# Revit family: RN 81033 Optipress-Aquaplus-Übergang
name_source: partatom
category: Rohrformteile
units: mm (PartAtom-declared; Revit-internal decimal feet)

## family parameters
Arbeitsebenenbasiert = Nein
Beim Laden mit Abzugskörper schneiden = Nein
Bemaßung runder Anschluss = Durchmesser verwenden
Gemeinsam genutzt = Nein
Immer vertikal = Ja
Teiletyp = Verbindung

## types (21) — shared parameters
1.010.00.2 Blattnummer der Richtlinie = 29
1.010.00.3 Ausgabedatum (Monat) der Richtlinie = 201308
1.010.00.4 Herstellername = R. Nussbaum AG
1.010.00.5 Revisionsdatum der Datei = 20190521
1.010.00.6 Webadresse des Herstellers = http://www.nussbaum.ch
1.100.00.4 Produktbezeichnung = Versorgung
1.110.00.2 Index = 4
1.110.00.4 Produktbezeichnung = Optipress
1.960/3L.00.8 Link (URL) = https://www.nussbaum.ch
29.700.00.4 Produktname = Optipress-Aquaplus-Übergang, mit Innengewinde
29.700.00.5 Produktkennung = 2
29.700.00.6 Querschnittsform = 1
29.700.00.7 Nennweitensystem = DN
29.700.00.8 Nenndrucksystem = PN
29.710.02.4 Nenndruck = 16
29.710.02.5 max. zul. Überdruck [hPa] = 1600
29.710.02.7 max. zul. Dauer-Betriebsdruck [hPa] = 1600
29.710.02.9 max. zul. Dauer-Betriebstemperatur [°C] = 95
Connector Visibility = Nein
EnclosingSpace Visibility = Nein

## per-type parameters (varying)
- 81033.19, Optipress-Aquaplus-Übergang, mit Innengewinde, DN=10, L=32, Rp=3/8: 1.800.00.3 TGA-Nummer=01900400000000000000000000000000000000000000000022000000000000000019; 1.810.00.3 Hersteller-Bestellnummer=81033.19; 1.810.00.4 DATANORM-Nummer=81033.19; 1.810.00.6 GTIN-Nummer=7612945021304; 29.710.02.10 Formstück-Gewicht [kg]=0.031; 29.710.02.3 Benennung=Optipress-Aquaplus-Übergang, mit Innengewinde, DN=10, L=32, Rp=3/8; CONNECTOR0_DIAMETER_dX_0r=10 mm  [stored 0.0328084 ft]; CONNECTOR0_dX_01=18 mm; CONNECTOR0_ref_dX=18 mm; CONNECTOR1_DIAMETER_dX_0r=10 mm  [stored 0.0328084 ft]; CONNECTOR1_dX_00=20 mm; CONNECTOR1_dX_01=32 mm; CONNECTOR1_ref_dX=20 mm; R. Nussbaum AG 81033.19 de Visibility=Ja; R. Nussbaum AG 81033.20 de Visibility=Nein; R. Nussbaum AG 81033.21 de Visibility=Nein; R. Nussbaum AG 81033.22 de Visibility=Nein; R. Nussbaum AG 81033.23 de Visibility=Nein; R. Nussbaum AG 81033.24 de Visibility=Nein; R. Nussbaum AG 81033.25 de Visibility=Nein; R. Nussbaum AG 81033.26 de Visibility=Nein; R. Nussbaum AG 81033.27 de Visibility=Nein; R. Nussbaum AG 81033.28 de Visibility=Nein; R. Nussbaum AG 81033.29 de Visibility=Nein; R. Nussbaum AG 81033.30 de Visibility=Nein; R. Nussbaum AG 81033.31 de Visibility=Nein; R. Nussbaum AG 81033.32 de Visibility=Nein; R. Nussbaum AG 81033.33 de Visibility=Nein; R. Nussbaum AG 81033.34 de Visibility=Nein; R. Nussbaum AG 81033.35 de Visibility=Nein; R. Nussbaum AG 81033.36 de Visibility=Nein; R. Nussbaum AG 81033.37 de Visibility=Nein; R. Nussbaum AG 81033.38 de Visibility=Nein; R. Nussbaum AG 81033.39 de Visibility=Nein
- 81033.21, Optipress-Aquaplus-Übergang, mit Innengewinde, DN=15x10, L=37, Rp=3/8: 1.800.00.3 TGA-Nummer=01900400000000000000000000000000000000000000000022000000000000000020; 1.810.00.3 Hersteller-Bestellnummer=81033.21; 1.810.00.4 DATANORM-Nummer=81033.21; 1.810.00.6 GTIN-Nummer=7612945021328; 29.710.02.10 Formstück-Gewicht [kg]=0.037; 29.710.02.3 Benennung=Optipress-Aquaplus-Übergang, mit Innengewinde, DN=15x10, L=37, Rp=3/8; CONNECTOR0_DIAMETER_dX_0r=12 mm  [stored 0.0393701 ft]; CONNECTOR0_dX_01=22 mm; CONNECTOR0_ref_dX=22 mm; CONNECTOR1_DIAMETER_dX_0r=12 mm  [stored 0.0393701 ft]; CONNECTOR1_dX_00=27 mm; CONNECTOR1_dX_01=37 mm; CONNECTOR1_ref_dX=27 mm; R. Nussbaum AG 81033.19 de Visibility=Nein; R. Nussbaum AG 81033.20 de Visibility=Nein; R. Nussbaum AG 81033.21 de Visibility=Ja; R. Nussbaum AG 81033.22 de Visibility=Nein; R. Nussbaum AG 81033.23 de Visibility=Nein; R. Nussbaum AG 81033.24 de Visibility=Nein; R. Nussbaum AG 81033.25 de Visibility=Nein; R. Nussbaum AG 81033.26 de Visibility=Nein; R. Nussbaum AG 81033.27 de Visibility=Nein; R. Nussbaum AG 81033.28 de Visibility=Nein; R. Nussbaum AG 81033.29 de Visibility=Nein; R. Nussbaum AG 81033.30 de Visibility=Nein; R. Nussbaum AG 81033.31 de Visibility=Nein; R. Nussbaum AG 81033.32 de Visibility=Nein; R. Nussbaum AG 81033.33 de Visibility=Nein; R. Nussbaum AG 81033.34 de Visibility=Nein; R. Nussbaum AG 81033.35 de Visibility=Nein; R. Nussbaum AG 81033.36 de Visibility=Nein; R. Nussbaum AG 81033.37 de Visibility=Nein; R. Nussbaum AG 81033.38 de Visibility=Nein; R. Nussbaum AG 81033.39 de Visibility=Nein
- 81033.22, Optipress-Aquaplus-Übergang, mit Innengewinde, DN=12x15, L=44, Rp=½: 1.800.00.3 TGA-Nummer=01900400000000000000000000000000000000000000000022000000000000000021; 1.810.00.3 Hersteller-Bestellnummer=81033.22; 1.810.00.4 DATANORM-Nummer=81033.22; 1.810.00.5 StLB-Nummer=267.132; 1.810.00.6 GTIN-Nummer=7612945021335; 29.710.02.10 Formstück-Gewicht [kg]=0.062; 29.710.02.3 Benennung=Optipress-Aquaplus-Übergang, mit Innengewinde, DN=12x15, L=44, Rp=½; CONNECTOR0_DIAMETER_dX_0r=12 mm  [stored 0.0393701 ft]; CONNECTOR0_dX_01=22 mm; CONNECTOR0_ref_dX=22 mm; CONNECTOR1_DIAMETER_dX_0r=15 mm; CONNECTOR1_dX_00=31 mm  [stored 0.101706 ft]; CONNECTOR1_dX_01=44 mm; CONNECTOR1_ref_dX=31 mm  [stored 0.101706 ft]; R. Nussbaum AG 81033.19 de Visibility=Nein; R. Nussbaum AG 81033.20 de Visibility=Nein; R. Nussbaum AG 81033.21 de Visibility=Nein; R. Nussbaum AG 81033.22 de Visibility=Ja; R. Nussbaum AG 81033.23 de Visibility=Nein; R. Nussbaum AG 81033.24 de Visibility=Nein; R. Nussbaum AG 81033.25 de Visibility=Nein; R. Nussbaum AG 81033.26 de Visibility=Nein; R. Nussbaum AG 81033.27 de Visibility=Nein; R. Nussbaum AG 81033.28 de Visibility=Nein; R. Nussbaum AG 81033.29 de Visibility=Nein; R. Nussbaum AG 81033.30 de Visibility=Nein; R. Nussbaum AG 81033.31 de Visibility=Nein; R. Nussbaum AG 81033.32 de Visibility=Nein; R. Nussbaum AG 81033.33 de Visibility=Nein; R. Nussbaum AG 81033.34 de Visibility=Nein; R. Nussbaum AG 81033.35 de Visibility=Nein; R. Nussbaum AG 81033.36 de Visibility=Nein; R. Nussbaum AG 81033.37 de Visibility=Nein; R. Nussbaum AG 81033.38 de Visibility=Nein; R. Nussbaum AG 81033.39 de Visibility=Nein
- 81033.23, Optipress-Aquaplus-Übergang, mit Innengewinde, DN=15, L=43, Rp=½: 1.800.00.3 TGA-Nummer=01900400000000000000000000000000000000000000000022000000000000000022; 1.810.00.3 Hersteller-Bestellnummer=81033.23; 1.810.00.4 DATANORM-Nummer=81033.23; 1.810.00.5 StLB-Nummer=267.133; 1.810.00.6 GTIN-Nummer=7612945021342; 29.710.02.10 Formstück-Gewicht [kg]=0.063; 29.710.02.3 Benennung=Optipress-Aquaplus-Übergang, mit Innengewinde, DN=15, L=43, Rp=½; CONNECTOR0_DIAMETER_dX_0r=15 mm; CONNECTOR0_dX_01=22 mm; CONNECTOR0_ref_dX=22 mm; CONNECTOR1_DIAMETER_dX_0r=15 mm; CONNECTOR1_dX_00=30 mm  [stored 0.0984252 ft]; CONNECTOR1_dX_01=43 mm  [stored 0.141076 ft]; CONNECTOR1_ref_dX=30 mm  [stored 0.0984252 ft]; R. Nussbaum AG 81033.19 de Visibility=Nein; R. Nussbaum AG 81033.20 de Visibility=Nein; R. Nussbaum AG 81033.21 de Visibility=Nein; R. Nussbaum AG 81033.22 de Visibility=Nein; R. Nussbaum AG 81033.23 de Visibility=Ja; R. Nussbaum AG 81033.24 de Visibility=Nein; R. Nussbaum AG 81033.25 de Visibility=Nein; R. Nussbaum AG 81033.26 de Visibility=Nein; R. Nussbaum AG 81033.27 de Visibility=Nein; R. Nussbaum AG 81033.28 de Visibility=Nein; R. Nussbaum AG 81033.29 de Visibility=Nein; R. Nussbaum AG 81033.30 de Visibility=Nein; R. Nussbaum AG 81033.31 de Visibility=Nein; R. Nussbaum AG 81033.32 de Visibility=Nein; R. Nussbaum AG 81033.33 de Visibility=Nein; R. Nussbaum AG 81033.34 de Visibility=Nein; R. Nussbaum AG 81033.35 de Visibility=Nein; R. Nussbaum AG 81033.36 de Visibility=Nein; R. Nussbaum AG 81033.37 de Visibility=Nein; R. Nussbaum AG 81033.38 de Visibility=Nein; R. Nussbaum AG 81033.39 de Visibility=Nein
- 81033.24, Optipress-Aquaplus-Übergang, mit Innengewinde, DN=15x20, L=45, Rp=¾: 1.800.00.3 TGA-Nummer=01900400000000000000000000000000000000000000000022000000000000000023; 1.810.00.3 Hersteller-Bestellnummer=81033.24; 1.810.00.4 DATANORM-Nummer=81033.24; 1.810.00.6 GTIN-Nummer=7612945021359; 29.710.02.10 Formstück-Gewicht [kg]=0.076; 29.710.02.3 Benennung=Optipress-Aquaplus-Übergang, mit Innengewinde, DN=15x20, L=45, Rp=¾; CONNECTOR0_DIAMETER_dX_0r=15 mm; CONNECTOR0_dX_01=22 mm; CONNECTOR0_ref_dX=22 mm; CONNECTOR1_DIAMETER_dX_0r=20 mm; CONNECTOR1_dX_00=30 mm  [stored 0.0984252 ft]; CONNECTOR1_dX_01=45 mm; CONNECTOR1_ref_dX=30 mm  [stored 0.0984252 ft]; R. Nussbaum AG 81033.19 de Visibility=Nein; R. Nussbaum AG 81033.20 de Visibility=Nein; R. Nussbaum AG 81033.21 de Visibility=Nein; R. Nussbaum AG 81033.22 de Visibility=Nein; R. Nussbaum AG 81033.23 de Visibility=Nein; R. Nussbaum AG 81033.24 de Visibility=Ja; R. Nussbaum AG 81033.25 de Visibility=Nein; R. Nussbaum AG 81033.26 de Visibility=Nein; R. Nussbaum AG 81033.27 de Visibility=Nein; R. Nussbaum AG 81033.28 de Visibility=Nein; R. Nussbaum AG 81033.29 de Visibility=Nein; R. Nussbaum AG 81033.30 de Visibility=Nein; R. Nussbaum AG 81033.31 de Visibility=Nein; R. Nussbaum AG 81033.32 de Visibility=Nein; R. Nussbaum AG 81033.33 de Visibility=Nein; R. Nussbaum AG 81033.34 de Visibility=Nein; R. Nussbaum AG 81033.35 de Visibility=Nein; R. Nussbaum AG 81033.36 de Visibility=Nein; R. Nussbaum AG 81033.37 de Visibility=Nein; R. Nussbaum AG 81033.38 de Visibility=Nein; R. Nussbaum AG 81033.39 de Visibility=Nein
- 81033.25, Optipress-Aquaplus-Übergang, mit Innengewinde, DN=20, L=47, Rp=¾: 1.800.00.3 TGA-Nummer=01900400000000000000000000000000000000000000000022000000000000000024; 1.810.00.3 Hersteller-Bestellnummer=81033.25; 1.810.00.4 DATANORM-Nummer=81033.25; 1.810.00.5 StLB-Nummer=267.134; 1.810.00.6 GTIN-Nummer=7612945021366; 29.710.02.10 Formstück-Gewicht [kg]=0.082; 29.710.02.3 Benennung=Optipress-Aquaplus-Übergang, mit Innengewinde, DN=20, L=47, Rp=¾; CONNECTOR0_DIAMETER_dX_0r=20 mm; CONNECTOR0_dX_01=24 mm; CONNECTOR0_ref_dX=24 mm; CONNECTOR1_DIAMETER_dX_0r=20 mm; CONNECTOR1_dX_00=32 mm; CONNECTOR1_dX_01=47 mm; CONNECTOR1_ref_dX=32 mm; R. Nussbaum AG 81033.19 de Visibility=Nein; R. Nussbaum AG 81033.20 de Visibility=Nein; R. Nussbaum AG 81033.21 de Visibility=Nein; R. Nussbaum AG 81033.22 de Visibility=Nein; R. Nussbaum AG 81033.23 de Visibility=Nein; R. Nussbaum AG 81033.24 de Visibility=Nein; R. Nussbaum AG 81033.25 de Visibility=Ja; R. Nussbaum AG 81033.26 de Visibility=Nein; R. Nussbaum AG 81033.27 de Visibility=Nein; R. Nussbaum AG 81033.28 de Visibility=Nein; R. Nussbaum AG 81033.29 de Visibility=Nein; R. Nussbaum AG 81033.30 de Visibility=Nein; R. Nussbaum AG 81033.31 de Visibility=Nein; R. Nussbaum AG 81033.32 de Visibility=Nein; R. Nussbaum AG 81033.33 de Visibility=Nein; R. Nussbaum AG 81033.34 de Visibility=Nein; R. Nussbaum AG 81033.35 de Visibility=Nein; R. Nussbaum AG 81033.36 de Visibility=Nein; R. Nussbaum AG 81033.37 de Visibility=Nein; R. Nussbaum AG 81033.38 de Visibility=Nein; R. Nussbaum AG 81033.39 de Visibility=Nein
- 81033.26, Optipress-Aquaplus-Übergang, mit Innengewinde, DN=20x25, L=52, Rp=1: 1.800.00.3 TGA-Nummer=01900400000000000000000000000000000000000000000022000000000000000025; 1.810.00.3 Hersteller-Bestellnummer=81033.26; 1.810.00.4 DATANORM-Nummer=81033.26; 1.810.00.6 GTIN-Nummer=7612945021373; 29.710.02.10 Formstück-Gewicht [kg]=0.131; 29.710.02.3 Benennung=Optipress-Aquaplus-Übergang, mit Innengewinde, DN=20x25, L=52, Rp=1; CONNECTOR0_DIAMETER_dX_0r=20 mm; CONNECTOR0_dX_01=24 mm; CONNECTOR0_ref_dX=24 mm; CONNECTOR1_DIAMETER_dX_0r=25 mm  [stored 0.082021 ft]; CONNECTOR1_dX_00=35 mm; CONNECTOR1_dX_01=52 mm; CONNECTOR1_ref_dX=35 mm; R. Nussbaum AG 81033.19 de Visibility=Nein; R. Nussbaum AG 81033.20 de Visibility=Nein; R. Nussbaum AG 81033.21 de Visibility=Nein; R. Nussbaum AG 81033.22 de Visibility=Nein; R. Nussbaum AG 81033.23 de Visibility=Nein; R. Nussbaum AG 81033.24 de Visibility=Nein; R. Nussbaum AG 81033.25 de Visibility=Nein; R. Nussbaum AG 81033.26 de Visibility=Ja; R. Nussbaum AG 81033.27 de Visibility=Nein; R. Nussbaum AG 81033.28 de Visibility=Nein; R. Nussbaum AG 81033.29 de Visibility=Nein; R. Nussbaum AG 81033.30 de Visibility=Nein; R. Nussbaum AG 81033.31 de Visibility=Nein; R. Nussbaum AG 81033.32 de Visibility=Nein; R. Nussbaum AG 81033.33 de Visibility=Nein; R. Nussbaum AG 81033.34 de Visibility=Nein; R. Nussbaum AG 81033.35 de Visibility=Nein; R. Nussbaum AG 81033.36 de Visibility=Nein; R. Nussbaum AG 81033.37 de Visibility=Nein; R. Nussbaum AG 81033.38 de Visibility=Nein; R. Nussbaum AG 81033.39 de Visibility=Nein
- 81033.27, Optipress-Aquaplus-Übergang, mit Innengewinde, DN=25x20, L=47, Rp=¾: 1.800.00.3 TGA-Nummer=01900400000000000000000000000000000000000000000022000000000000000026; 1.810.00.3 Hersteller-Bestellnummer=81033.27; 1.810.00.4 DATANORM-Nummer=81033.27; 1.810.00.6 GTIN-Nummer=7612945021380; 29.710.02.10 Formstück-Gewicht [kg]=0.095; 29.710.02.3 Benennung=Optipress-Aquaplus-Übergang, mit Innengewinde, DN=25x20, L=47, Rp=¾; CONNECTOR0_DIAMETER_dX_0r=25 mm  [stored 0.082021 ft]; CONNECTOR0_dX_01=24 mm; CONNECTOR0_ref_dX=24 mm; CONNECTOR1_DIAMETER_dX_0r=20 mm; CONNECTOR1_dX_00=32 mm; CONNECTOR1_dX_01=47 mm; CONNECTOR1_ref_dX=32 mm; R. Nussbaum AG 81033.19 de Visibility=Nein; R. Nussbaum AG 81033.20 de Visibility=Nein; R. Nussbaum AG 81033.21 de Visibility=Nein; R. Nussbaum AG 81033.22 de Visibility=Nein; R. Nussbaum AG 81033.23 de Visibility=Nein; R. Nussbaum AG 81033.24 de Visibility=Nein; R. Nussbaum AG 81033.25 de Visibility=Nein; R. Nussbaum AG 81033.26 de Visibility=Nein; R. Nussbaum AG 81033.27 de Visibility=Ja; R. Nussbaum AG 81033.28 de Visibility=Nein; R. Nussbaum AG 81033.29 de Visibility=Nein; R. Nussbaum AG 81033.30 de Visibility=Nein; R. Nussbaum AG 81033.31 de Visibility=Nein; R. Nussbaum AG 81033.32 de Visibility=Nein; R. Nussbaum AG 81033.33 de Visibility=Nein; R. Nussbaum AG 81033.34 de Visibility=Nein; R. Nussbaum AG 81033.35 de Visibility=Nein; R. Nussbaum AG 81033.36 de Visibility=Nein; R. Nussbaum AG 81033.37 de Visibility=Nein; R. Nussbaum AG 81033.38 de Visibility=Nein; R. Nussbaum AG 81033.39 de Visibility=Nein
- 81033.28, Optipress-Aquaplus-Übergang, mit Innengewinde, DN=25x15, L=44, Rp=½: 1.800.00.3 TGA-Nummer=01900400000000000000000000000000000000000000000022000000000000000027; 1.810.00.3 Hersteller-Bestellnummer=81033.28; 1.810.00.4 DATANORM-Nummer=81033.28; 1.810.00.6 GTIN-Nummer=7612945682727; 29.710.02.10 Formstück-Gewicht [kg]=0.089; 29.710.02.3 Benennung=Optipress-Aquaplus-Übergang, mit Innengewinde, DN=25x15, L=44, Rp=½; CONNECTOR0_DIAMETER_dX_0r=25 mm  [stored 0.082021 ft]; CONNECTOR0_dX_01=24 mm; CONNECTOR0_ref_dX=24 mm; CONNECTOR1_DIAMETER_dX_0r=15 mm; CONNECTOR1_dX_00=31 mm  [stored 0.101706 ft]; CONNECTOR1_dX_01=44 mm; CONNECTOR1_ref_dX=31 mm  [stored 0.101706 ft]; R. Nussbaum AG 81033.19 de Visibility=Nein; R. Nussbaum AG 81033.20 de Visibility=Nein; R. Nussbaum AG 81033.21 de Visibility=Nein; R. Nussbaum AG 81033.22 de Visibility=Nein; R. Nussbaum AG 81033.23 de Visibility=Nein; R. Nussbaum AG 81033.24 de Visibility=Nein; R. Nussbaum AG 81033.25 de Visibility=Nein; R. Nussbaum AG 81033.26 de Visibility=Nein; R. Nussbaum AG 81033.27 de Visibility=Nein; R. Nussbaum AG 81033.28 de Visibility=Ja; R. Nussbaum AG 81033.29 de Visibility=Nein; R. Nussbaum AG 81033.30 de Visibility=Nein; R. Nussbaum AG 81033.31 de Visibility=Nein; R. Nussbaum AG 81033.32 de Visibility=Nein; R. Nussbaum AG 81033.33 de Visibility=Nein; R. Nussbaum AG 81033.34 de Visibility=Nein; R. Nussbaum AG 81033.35 de Visibility=Nein; R. Nussbaum AG 81033.36 de Visibility=Nein; R. Nussbaum AG 81033.37 de Visibility=Nein; R. Nussbaum AG 81033.38 de Visibility=Nein; R. Nussbaum AG 81033.39 de Visibility=Nein
- 81033.29, Optipress-Aquaplus-Übergang, mit Innengewinde, DN=20, L=52, Rp=1: 1.800.00.3 TGA-Nummer=01900400000000000000000000000000000000000000000022000000000000000028; 1.810.00.3 Hersteller-Bestellnummer=81033.29; 1.810.00.4 DATANORM-Nummer=81033.29; 1.810.00.5 StLB-Nummer=267.135; 1.810.00.6 GTIN-Nummer=7612945021397; 29.710.02.10 Formstück-Gewicht [kg]=0.124; 29.710.02.3 Benennung=Optipress-Aquaplus-Übergang, mit Innengewinde, DN=20, L=52, Rp=1; CONNECTOR0_DIAMETER_dX_0r=25 mm  [stored 0.082021 ft]; CONNECTOR0_dX_01=24 mm; CONNECTOR0_ref_dX=24 mm; CONNECTOR1_DIAMETER_dX_0r=25 mm  [stored 0.082021 ft]; CONNECTOR1_dX_00=35 mm; CONNECTOR1_dX_01=52 mm; CONNECTOR1_ref_dX=35 mm; R. Nussbaum AG 81033.19 de Visibility=Nein; R. Nussbaum AG 81033.20 de Visibility=Nein; R. Nussbaum AG 81033.21 de Visibility=Nein; R. Nussbaum AG 81033.22 de Visibility=Nein; R. Nussbaum AG 81033.23 de Visibility=Nein; R. Nussbaum AG 81033.24 de Visibility=Nein; R. Nussbaum AG 81033.25 de Visibility=Nein; R. Nussbaum AG 81033.26 de Visibility=Nein; R. Nussbaum AG 81033.27 de Visibility=Nein; R. Nussbaum AG 81033.28 de Visibility=Nein; R. Nussbaum AG 81033.29 de Visibility=Ja; R. Nussbaum AG 81033.30 de Visibility=Nein; R. Nussbaum AG 81033.31 de Visibility=Nein; R. Nussbaum AG 81033.32 de Visibility=Nein; R. Nussbaum AG 81033.33 de Visibility=Nein; R. Nussbaum AG 81033.34 de Visibility=Nein; R. Nussbaum AG 81033.35 de Visibility=Nein; R. Nussbaum AG 81033.36 de Visibility=Nein; R. Nussbaum AG 81033.37 de Visibility=Nein; R. Nussbaum AG 81033.38 de Visibility=Nein; R. Nussbaum AG 81033.39 de Visibility=Nein
- 81033.31, Optipress-Aquaplus-Übergang, mit Innengewinde, DN=32, L=54, Rp=1¼: 1.800.00.3 TGA-Nummer=01900400000000000000000000000000000000000000000022000000000000000029; 1.810.00.3 Hersteller-Bestellnummer=81033.31; 1.810.00.4 DATANORM-Nummer=81033.31; 1.810.00.5 StLB-Nummer=267.136; 1.810.00.6 GTIN-Nummer=7612945021410; 29.710.02.10 Formstück-Gewicht [kg]=0.17; 29.710.02.3 Benennung=Optipress-Aquaplus-Übergang, mit Innengewinde, DN=32, L=54, Rp=1¼; CONNECTOR0_DIAMETER_dX_0r=32 mm; CONNECTOR0_dX_01=26 mm; CONNECTOR0_ref_dX=26 mm; CONNECTOR1_DIAMETER_dX_0r=32 mm; CONNECTOR1_dX_00=35 mm; CONNECTOR1_dX_01=54 mm; CONNECTOR1_ref_dX=35 mm; R. Nussbaum AG 81033.19 de Visibility=Nein; R. Nussbaum AG 81033.20 de Visibility=Nein; R. Nussbaum AG 81033.21 de Visibility=Nein; R. Nussbaum AG 81033.22 de Visibility=Nein; R. Nussbaum AG 81033.23 de Visibility=Nein; R. Nussbaum AG 81033.24 de Visibility=Nein; R. Nussbaum AG 81033.25 de Visibility=Nein; R. Nussbaum AG 81033.26 de Visibility=Nein; R. Nussbaum AG 81033.27 de Visibility=Nein; R. Nussbaum AG 81033.28 de Visibility=Nein; R. Nussbaum AG 81033.29 de Visibility=Nein; R. Nussbaum AG 81033.30 de Visibility=Nein; R. Nussbaum AG 81033.31 de Visibility=Ja; R. Nussbaum AG 81033.32 de Visibility=Nein; R. Nussbaum AG 81033.33 de Visibility=Nein; R. Nussbaum AG 81033.34 de Visibility=Nein; R. Nussbaum AG 81033.35 de Visibility=Nein; R. Nussbaum AG 81033.36 de Visibility=Nein; R. Nussbaum AG 81033.37 de Visibility=Nein; R. Nussbaum AG 81033.38 de Visibility=Nein; R. Nussbaum AG 81033.39 de Visibility=Nein
- 81033.32, Optipress-Aquaplus-Übergang, mit Innengewinde, DN=40x32, L=61, Rp=1¼: 1.800.00.3 TGA-Nummer=01900400000000000000000000000000000000000000000022000000000000000030; 1.810.00.3 Hersteller-Bestellnummer=81033.32; 1.810.00.4 DATANORM-Nummer=81033.32; 1.810.00.6 GTIN-Nummer=7612945021427; 29.710.02.10 Formstück-Gewicht [kg]=0.22; 29.710.02.3 Benennung=Optipress-Aquaplus-Übergang, mit Innengewinde, DN=40x32, L=61, Rp=1¼; CONNECTOR0_DIAMETER_dX_0r=40 mm; CONNECTOR0_dX_01=36 mm; CONNECTOR0_ref_dX=36 mm; CONNECTOR1_DIAMETER_dX_0r=32 mm; CONNECTOR1_dX_00=42 mm; CONNECTOR1_dX_01=61 mm; CONNECTOR1_ref_dX=42 mm; R. Nussbaum AG 81033.19 de Visibility=Nein; R. Nussbaum AG 81033.20 de Visibility=Nein; R. Nussbaum AG 81033.21 de Visibility=Nein; R. Nussbaum AG 81033.22 de Visibility=Nein; R. Nussbaum AG 81033.23 de Visibility=Nein; R. Nussbaum AG 81033.24 de Visibility=Nein; R. Nussbaum AG 81033.25 de Visibility=Nein; R. Nussbaum AG 81033.26 de Visibility=Nein; R. Nussbaum AG 81033.27 de Visibility=Nein; R. Nussbaum AG 81033.28 de Visibility=Nein; R. Nussbaum AG 81033.29 de Visibility=Nein; R. Nussbaum AG 81033.30 de Visibility=Nein; R. Nussbaum AG 81033.31 de Visibility=Nein; R. Nussbaum AG 81033.32 de Visibility=Ja; R. Nussbaum AG 81033.33 de Visibility=Nein; R. Nussbaum AG 81033.34 de Visibility=Nein; R. Nussbaum AG 81033.35 de Visibility=Nein; R. Nussbaum AG 81033.36 de Visibility=Nein; R. Nussbaum AG 81033.37 de Visibility=Nein; R. Nussbaum AG 81033.38 de Visibility=Nein; R. Nussbaum AG 81033.39 de Visibility=Nein
- 81033.33, Optipress-Aquaplus-Übergang, mit Innengewinde, DN=40, L=69, Rp=1½: 1.800.00.3 TGA-Nummer=01900400000000000000000000000000000000000000000022000000000000000031; 1.810.00.3 Hersteller-Bestellnummer=81033.33; 1.810.00.4 DATANORM-Nummer=81033.33; 1.810.00.5 StLB-Nummer=267.137; 1.810.00.6 GTIN-Nummer=7612945021434; 29.710.02.10 Formstück-Gewicht [kg]=0.267; 29.710.02.3 Benennung=Optipress-Aquaplus-Übergang, mit Innengewinde, DN=40, L=69, Rp=1½; CONNECTOR0_DIAMETER_dX_0r=40 mm; CONNECTOR0_dX_01=36 mm; CONNECTOR0_ref_dX=36 mm; CONNECTOR1_DIAMETER_dX_0r=32 mm; CONNECTOR1_dX_00=50 mm; CONNECTOR1_dX_01=69 mm; CONNECTOR1_ref_dX=50 mm; R. Nussbaum AG 81033.19 de Visibility=Nein; R. Nussbaum AG 81033.20 de Visibility=Nein; R. Nussbaum AG 81033.21 de Visibility=Nein; R. Nussbaum AG 81033.22 de Visibility=Nein; R. Nussbaum AG 81033.23 de Visibility=Nein; R. Nussbaum AG 81033.24 de Visibility=Nein; R. Nussbaum AG 81033.25 de Visibility=Nein; R. Nussbaum AG 81033.26 de Visibility=Nein; R. Nussbaum AG 81033.27 de Visibility=Nein; R. Nussbaum AG 81033.28 de Visibility=Nein; R. Nussbaum AG 81033.29 de Visibility=Nein; R. Nussbaum AG 81033.30 de Visibility=Nein; R. Nussbaum AG 81033.31 de Visibility=Nein; R. Nussbaum AG 81033.32 de Visibility=Nein; R. Nussbaum AG 81033.33 de Visibility=Ja; R. Nussbaum AG 81033.34 de Visibility=Nein; R. Nussbaum AG 81033.35 de Visibility=Nein; R. Nussbaum AG 81033.36 de Visibility=Nein; R. Nussbaum AG 81033.37 de Visibility=Nein; R. Nussbaum AG 81033.38 de Visibility=Nein; R. Nussbaum AG 81033.39 de Visibility=Nein
- 81033.34, Optipress-Aquaplus-Übergang, mit Innengewinde, DN=50x40, L=71, Rp=1½: 1.800.00.3 TGA-Nummer=01900400000000000000000000000000000000000000000022000000000000000032; 1.810.00.3 Hersteller-Bestellnummer=81033.34; 1.810.00.4 DATANORM-Nummer=81033.34; 1.810.00.6 GTIN-Nummer=7612945682734; 29.710.02.10 Formstück-Gewicht [kg]=0.442; 29.710.02.3 Benennung=Optipress-Aquaplus-Übergang, mit Innengewinde, DN=50x40, L=71, Rp=1½; CONNECTOR0_DIAMETER_dX_0r=50 mm; CONNECTOR0_dX_01=40 mm; CONNECTOR0_ref_dX=40 mm; CONNECTOR1_DIAMETER_dX_0r=40 mm; CONNECTOR1_dX_00=53 mm; CONNECTOR1_dX_01=72 mm; CONNECTOR1_ref_dX=53 mm; R. Nussbaum AG 81033.19 de Visibility=Nein; R. Nussbaum AG 81033.20 de Visibility=Nein; R. Nussbaum AG 81033.21 de Visibility=Nein; R. Nussbaum AG 81033.22 de Visibility=Nein; R. Nussbaum AG 81033.23 de Visibility=Nein; R. Nussbaum AG 81033.24 de Visibility=Nein; R. Nussbaum AG 81033.25 de Visibility=Nein; R. Nussbaum AG 81033.26 de Visibility=Nein; R. Nussbaum AG 81033.27 de Visibility=Nein; R. Nussbaum AG 81033.28 de Visibility=Nein; R. Nussbaum AG 81033.29 de Visibility=Nein; R. Nussbaum AG 81033.30 de Visibility=Nein; R. Nussbaum AG 81033.31 de Visibility=Nein; R. Nussbaum AG 81033.32 de Visibility=Nein; R. Nussbaum AG 81033.33 de Visibility=Nein; R. Nussbaum AG 81033.34 de Visibility=Ja; R. Nussbaum AG 81033.35 de Visibility=Nein; R. Nussbaum AG 81033.36 de Visibility=Nein; R. Nussbaum AG 81033.37 de Visibility=Nein; R. Nussbaum AG 81033.38 de Visibility=Nein; R. Nussbaum AG 81033.39 de Visibility=Nein
- 81033.35, Optipress-Aquaplus-Übergang, mit Innengewinde, DN=50, L=75, Rp=2: 1.800.00.3 TGA-Nummer=01900400000000000000000000000000000000000000000022000000000000000033; 1.810.00.3 Hersteller-Bestellnummer=81033.35; 1.810.00.4 DATANORM-Nummer=81033.35; 1.810.00.5 StLB-Nummer=267.138; 1.810.00.6 GTIN-Nummer=7612945021441; 29.710.02.10 Formstück-Gewicht [kg]=0.461; 29.710.02.3 Benennung=Optipress-Aquaplus-Übergang, mit Innengewinde, DN=50, L=75, Rp=2; CONNECTOR0_DIAMETER_dX_0r=50 mm; CONNECTOR0_dX_01=40 mm; CONNECTOR0_ref_dX=40 mm; CONNECTOR1_DIAMETER_dX_0r=50 mm; CONNECTOR1_dX_00=51 mm; CONNECTOR1_dX_01=75 mm; CONNECTOR1_ref_dX=51 mm; R. Nussbaum AG 81033.19 de Visibility=Nein; R. Nussbaum AG 81033.20 de Visibility=Nein; R. Nussbaum AG 81033.21 de Visibility=Nein; R. Nussbaum AG 81033.22 de Visibility=Nein; R. Nussbaum AG 81033.23 de Visibility=Nein; R. Nussbaum AG 81033.24 de Visibility=Nein; R. Nussbaum AG 81033.25 de Visibility=Nein; R. Nussbaum AG 81033.26 de Visibility=Nein; R. Nussbaum AG 81033.27 de Visibility=Nein; R. Nussbaum AG 81033.28 de Visibility=Nein; R. Nussbaum AG 81033.29 de Visibility=Nein; R. Nussbaum AG 81033.30 de Visibility=Nein; R. Nussbaum AG 81033.31 de Visibility=Nein; R. Nussbaum AG 81033.32 de Visibility=Nein; R. Nussbaum AG 81033.33 de Visibility=Nein; R. Nussbaum AG 81033.34 de Visibility=Nein; R. Nussbaum AG 81033.35 de Visibility=Ja; R. Nussbaum AG 81033.36 de Visibility=Nein; R. Nussbaum AG 81033.37 de Visibility=Nein; R. Nussbaum AG 81033.38 de Visibility=Nein; R. Nussbaum AG 81033.39 de Visibility=Nein
- 81033.36, Optipress-Aquaplus-Übergang, mit Innengewinde, DN=15x20, L=45, Rp=¾: 1.800.00.3 TGA-Nummer=01900400000000000000000000000000000000000000000022000000000000000034; 1.810.00.3 Hersteller-Bestellnummer=81033.36; 1.810.00.4 DATANORM-Nummer=81033.36; 1.810.00.6 GTIN-Nummer=7612945021458; 29.710.02.10 Formstück-Gewicht [kg]=0.071; 29.710.02.3 Benennung=Optipress-Aquaplus-Übergang, mit Innengewinde, DN=15x20, L=45, Rp=¾; CONNECTOR0_DIAMETER_dX_0r=15 mm; CONNECTOR0_dX_01=22 mm; CONNECTOR0_ref_dX=22 mm; CONNECTOR1_DIAMETER_dX_0r=20 mm; CONNECTOR1_dX_00=30 mm  [stored 0.0984252 ft]; CONNECTOR1_dX_01=45 mm; CONNECTOR1_ref_dX=30 mm  [stored 0.0984252 ft]; R. Nussbaum AG 81033.19 de Visibility=Nein; R. Nussbaum AG 81033.20 de Visibility=Nein; R. Nussbaum AG 81033.21 de Visibility=Nein; R. Nussbaum AG 81033.22 de Visibility=Nein; R. Nussbaum AG 81033.23 de Visibility=Nein; R. Nussbaum AG 81033.24 de Visibility=Nein; R. Nussbaum AG 81033.25 de Visibility=Nein; R. Nussbaum AG 81033.26 de Visibility=Nein; R. Nussbaum AG 81033.27 de Visibility=Nein; R. Nussbaum AG 81033.28 de Visibility=Nein; R. Nussbaum AG 81033.29 de Visibility=Nein; R. Nussbaum AG 81033.30 de Visibility=Nein; R. Nussbaum AG 81033.31 de Visibility=Nein; R. Nussbaum AG 81033.32 de Visibility=Nein; R. Nussbaum AG 81033.33 de Visibility=Nein; R. Nussbaum AG 81033.34 de Visibility=Nein; R. Nussbaum AG 81033.35 de Visibility=Nein; R. Nussbaum AG 81033.36 de Visibility=Ja; R. Nussbaum AG 81033.37 de Visibility=Nein; R. Nussbaum AG 81033.38 de Visibility=Nein; R. Nussbaum AG 81033.39 de Visibility=Nein
- 81033.37, Optipress-Aquaplus-Übergang, mit Innengewinde, DN=20x15, L=44, Rp=½: 1.800.00.3 TGA-Nummer=01900400000000000000000000000000000000000000000022000000000000000035; 1.810.00.3 Hersteller-Bestellnummer=81033.37; 1.810.00.4 DATANORM-Nummer=81033.37; 1.810.00.6 GTIN-Nummer=7612945021465; 29.710.02.10 Formstück-Gewicht [kg]=0.07; 29.710.02.3 Benennung=Optipress-Aquaplus-Übergang, mit Innengewinde, DN=20x15, L=44, Rp=½; CONNECTOR0_DIAMETER_dX_0r=20 mm; CONNECTOR0_dX_01=24 mm; CONNECTOR0_ref_dX=24 mm; CONNECTOR1_DIAMETER_dX_0r=15 mm; CONNECTOR1_dX_00=31 mm  [stored 0.101706 ft]; CONNECTOR1_dX_01=44 mm; CONNECTOR1_ref_dX=31 mm  [stored 0.101706 ft]; R. Nussbaum AG 81033.19 de Visibility=Nein; R. Nussbaum AG 81033.20 de Visibility=Nein; R. Nussbaum AG 81033.21 de Visibility=Nein; R. Nussbaum AG 81033.22 de Visibility=Nein; R. Nussbaum AG 81033.23 de Visibility=Nein; R. Nussbaum AG 81033.24 de Visibility=Nein; R. Nussbaum AG 81033.25 de Visibility=Nein; R. Nussbaum AG 81033.26 de Visibility=Nein; R. Nussbaum AG 81033.27 de Visibility=Nein; R. Nussbaum AG 81033.28 de Visibility=Nein; R. Nussbaum AG 81033.29 de Visibility=Nein; R. Nussbaum AG 81033.30 de Visibility=Nein; R. Nussbaum AG 81033.31 de Visibility=Nein; R. Nussbaum AG 81033.32 de Visibility=Nein; R. Nussbaum AG 81033.33 de Visibility=Nein; R. Nussbaum AG 81033.34 de Visibility=Nein; R. Nussbaum AG 81033.35 de Visibility=Nein; R. Nussbaum AG 81033.36 de Visibility=Nein; R. Nussbaum AG 81033.37 de Visibility=Ja; R. Nussbaum AG 81033.38 de Visibility=Nein; R. Nussbaum AG 81033.39 de Visibility=Nein
- 81033.38, Optipress-Aquaplus-Übergang, mit Innengewinde, DN=32x25, L=48, Rp=1: 1.800.00.3 TGA-Nummer=01900400000000000000000000000000000000000000000022000000000000000036; 1.810.00.3 Hersteller-Bestellnummer=81033.38; 1.810.00.4 DATANORM-Nummer=81033.38; 1.810.00.6 GTIN-Nummer=7612945021472; 29.710.02.10 Formstück-Gewicht [kg]=0.119; 29.710.02.3 Benennung=Optipress-Aquaplus-Übergang, mit Innengewinde, DN=32x25, L=48, Rp=1; CONNECTOR0_DIAMETER_dX_0r=32 mm; CONNECTOR0_dX_01=26 mm; CONNECTOR0_ref_dX=26 mm; CONNECTOR1_DIAMETER_dX_0r=25 mm  [stored 0.082021 ft]; CONNECTOR1_dX_00=31 mm  [stored 0.101706 ft]; CONNECTOR1_dX_01=48 mm; CONNECTOR1_ref_dX=31 mm  [stored 0.101706 ft]; R. Nussbaum AG 81033.19 de Visibility=Nein; R. Nussbaum AG 81033.20 de Visibility=Nein; R. Nussbaum AG 81033.21 de Visibility=Nein; R. Nussbaum AG 81033.22 de Visibility=Nein; R. Nussbaum AG 81033.23 de Visibility=Nein; R. Nussbaum AG 81033.24 de Visibility=Nein; R. Nussbaum AG 81033.25 de Visibility=Nein; R. Nussbaum AG 81033.26 de Visibility=Nein; R. Nussbaum AG 81033.27 de Visibility=Nein; R. Nussbaum AG 81033.28 de Visibility=Nein; R. Nussbaum AG 81033.29 de Visibility=Nein; R. Nussbaum AG 81033.30 de Visibility=Nein; R. Nussbaum AG 81033.31 de Visibility=Nein; R. Nussbaum AG 81033.32 de Visibility=Nein; R. Nussbaum AG 81033.33 de Visibility=Nein; R. Nussbaum AG 81033.34 de Visibility=Nein; R. Nussbaum AG 81033.35 de Visibility=Nein; R. Nussbaum AG 81033.36 de Visibility=Nein; R. Nussbaum AG 81033.37 de Visibility=Nein; R. Nussbaum AG 81033.38 de Visibility=Ja; R. Nussbaum AG 81033.39 de Visibility=Nein
- 81033.39, Optipress-Aquaplus-Übergang, mit Innengewinde, DN=32x20, L=47, Rp=¾: 1.800.00.3 TGA-Nummer=01900400000000000000000000000000000000000000000022000000000000000037; 1.810.00.3 Hersteller-Bestellnummer=81033.39; 1.810.00.4 DATANORM-Nummer=81033.39; 1.810.00.6 GTIN-Nummer=7612945021489; 29.710.02.10 Formstück-Gewicht [kg]=0.111; 29.710.02.3 Benennung=Optipress-Aquaplus-Übergang, mit Innengewinde, DN=32x20, L=47, Rp=¾; CONNECTOR0_DIAMETER_dX_0r=32 mm; CONNECTOR0_dX_01=26 mm; CONNECTOR0_ref_dX=26 mm; CONNECTOR1_DIAMETER_dX_0r=20 mm; CONNECTOR1_dX_00=32 mm; CONNECTOR1_dX_01=47 mm; CONNECTOR1_ref_dX=32 mm; R. Nussbaum AG 81033.19 de Visibility=Nein; R. Nussbaum AG 81033.20 de Visibility=Nein; R. Nussbaum AG 81033.21 de Visibility=Nein; R. Nussbaum AG 81033.22 de Visibility=Nein; R. Nussbaum AG 81033.23 de Visibility=Nein; R. Nussbaum AG 81033.24 de Visibility=Nein; R. Nussbaum AG 81033.25 de Visibility=Nein; R. Nussbaum AG 81033.26 de Visibility=Nein; R. Nussbaum AG 81033.27 de Visibility=Nein; R. Nussbaum AG 81033.28 de Visibility=Nein; R. Nussbaum AG 81033.29 de Visibility=Nein; R. Nussbaum AG 81033.30 de Visibility=Nein; R. Nussbaum AG 81033.31 de Visibility=Nein; R. Nussbaum AG 81033.32 de Visibility=Nein; R. Nussbaum AG 81033.33 de Visibility=Nein; R. Nussbaum AG 81033.34 de Visibility=Nein; R. Nussbaum AG 81033.35 de Visibility=Nein; R. Nussbaum AG 81033.36 de Visibility=Nein; R. Nussbaum AG 81033.37 de Visibility=Nein; R. Nussbaum AG 81033.38 de Visibility=Nein; R. Nussbaum AG 81033.39 de Visibility=Ja
- 81033.20, Optipress-Aquaplus-Übergang, mit Innengewinde, DN=10x15, L=39, Rp=½: 1.800.00.3 TGA-Nummer=01900400000000000000000000000000000000000000000022000000000000000040; 1.810.00.3 Hersteller-Bestellnummer=81033.20; 1.810.00.4 DATANORM-Nummer=81033.20; 1.810.00.5 StLB-Nummer=267.131; 1.810.00.6 GTIN-Nummer=7612945021311; 29.710.02.10 Formstück-Gewicht [kg]=0.054; 29.710.02.3 Benennung=Optipress-Aquaplus-Übergang, mit Innengewinde, DN=10x15, L=39, Rp=½; CONNECTOR0_DIAMETER_dX_0r=10 mm  [stored 0.0328084 ft]; CONNECTOR0_dX_01=18 mm; CONNECTOR0_ref_dX=18 mm; CONNECTOR1_DIAMETER_dX_0r=15 mm; CONNECTOR1_dX_00=26 mm; CONNECTOR1_dX_01=39 mm; CONNECTOR1_ref_dX=26 mm; R. Nussbaum AG 81033.19 de Visibility=Nein; R. Nussbaum AG 81033.20 de Visibility=Ja; R. Nussbaum AG 81033.21 de Visibility=Nein; R. Nussbaum AG 81033.22 de Visibility=Nein; R. Nussbaum AG 81033.23 de Visibility=Nein; R. Nussbaum AG 81033.24 de Visibility=Nein; R. Nussbaum AG 81033.25 de Visibility=Nein; R. Nussbaum AG 81033.26 de Visibility=Nein; R. Nussbaum AG 81033.27 de Visibility=Nein; R. Nussbaum AG 81033.28 de Visibility=Nein; R. Nussbaum AG 81033.29 de Visibility=Nein; R. Nussbaum AG 81033.30 de Visibility=Nein; R. Nussbaum AG 81033.31 de Visibility=Nein; R. Nussbaum AG 81033.32 de Visibility=Nein; R. Nussbaum AG 81033.33 de Visibility=Nein; R. Nussbaum AG 81033.34 de Visibility=Nein; R. Nussbaum AG 81033.35 de Visibility=Nein; R. Nussbaum AG 81033.36 de Visibility=Nein; R. Nussbaum AG 81033.37 de Visibility=Nein; R. Nussbaum AG 81033.38 de Visibility=Nein; R. Nussbaum AG 81033.39 de Visibility=Nein
- 81033.30, Optipress-Aquaplus-Übergang, mit Innengewinde, DN=25x32, L=55, Rp=1¼: 1.800.00.3 TGA-Nummer=01900400000000000000000000000000000000000000000022000000000000000041; 1.810.00.3 Hersteller-Bestellnummer=81033.30; 1.810.00.4 DATANORM-Nummer=81033.30; 1.810.00.6 GTIN-Nummer=7612945021403; 29.710.02.10 Formstück-Gewicht [kg]=0.161; 29.710.02.3 Benennung=Optipress-Aquaplus-Übergang, mit Innengewinde, DN=25x32, L=55, Rp=1¼; CONNECTOR0_DIAMETER_dX_0r=25 mm  [stored 0.082021 ft]; CONNECTOR0_dX_01=24 mm; CONNECTOR0_ref_dX=24 mm; CONNECTOR1_DIAMETER_dX_0r=32 mm; CONNECTOR1_dX_00=36 mm; CONNECTOR1_dX_01=55 mm; CONNECTOR1_ref_dX=36 mm; R. Nussbaum AG 81033.19 de Visibility=Nein; R. Nussbaum AG 81033.20 de Visibility=Nein; R. Nussbaum AG 81033.21 de Visibility=Nein; R. Nussbaum AG 81033.22 de Visibility=Nein; R. Nussbaum AG 81033.23 de Visibility=Nein; R. Nussbaum AG 81033.24 de Visibility=Nein; R. Nussbaum AG 81033.25 de Visibility=Nein; R. Nussbaum AG 81033.26 de Visibility=Nein; R. Nussbaum AG 81033.27 de Visibility=Nein; R. Nussbaum AG 81033.28 de Visibility=Nein; R. Nussbaum AG 81033.29 de Visibility=Nein; R. Nussbaum AG 81033.30 de Visibility=Ja; R. Nussbaum AG 81033.31 de Visibility=Nein; R. Nussbaum AG 81033.32 de Visibility=Nein; R. Nussbaum AG 81033.33 de Visibility=Nein; R. Nussbaum AG 81033.34 de Visibility=Nein; R. Nussbaum AG 81033.35 de Visibility=Nein; R. Nussbaum AG 81033.36 de Visibility=Nein; R. Nussbaum AG 81033.37 de Visibility=Nein; R. Nussbaum AG 81033.38 de Visibility=Nein; R. Nussbaum AG 81033.39 de Visibility=Nein

note: column(s) folded — value = type name in every type: 1.800.00.4 Kommentarfeld

note: [stored X ft] marks values corroborated as IEEE doubles in the binary element streams (Revit-internal decimal feet)

## geometry (parser evidence)
native form markers: Sweep x3
no freeform markers — native parametric forms only
